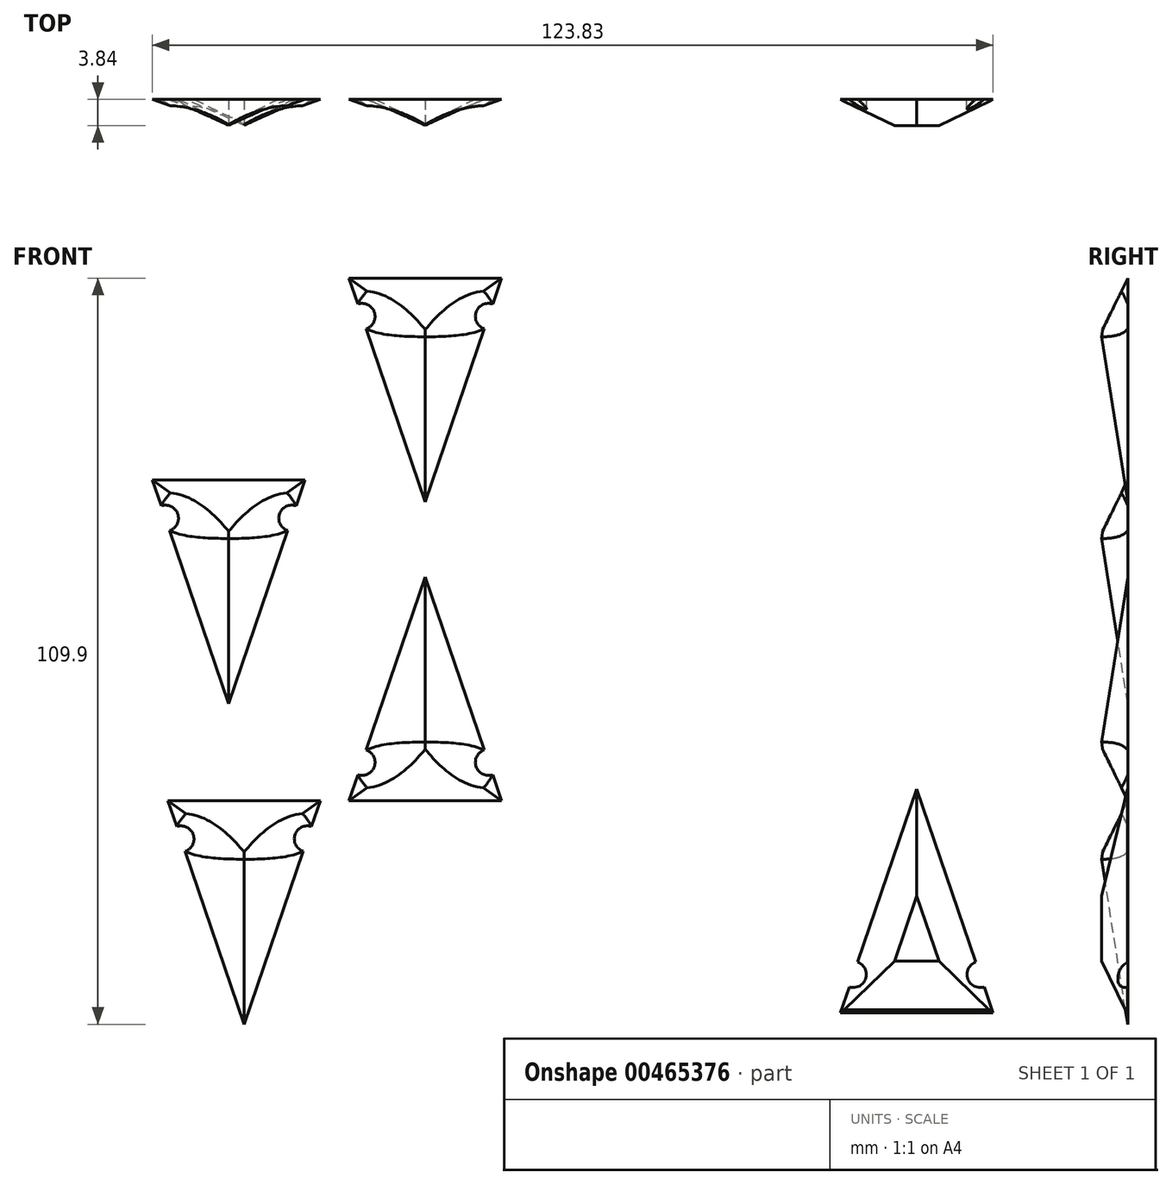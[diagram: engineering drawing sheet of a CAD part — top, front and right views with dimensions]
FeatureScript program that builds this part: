
annotation { "Feature Type Name" : "Feature", "Feature Type Description" : "" }
export const myFeature = defineFeature(function(context is Context, id is Id, definition is map)
    precondition{}
    {
        {
            var Q0;
            Q0=qCreatedBy(makeId("Front.planeOp"),FACE);
            var sketch = newSketch(context, id + "F0", { "sketchPlane" : qUnion([Q0])});
            skLineSegment(sketch, "E0.0", {"start": v(51.45, -35.1) * mm, "end": v(28.97, -35.1) * mm});
            skPoint(sketch, "E0.0.midPoint", {"position": v(40.22, -35.1) * mm});
            skPoint(sketch, "E0.cCircle.center.orphan", {"position": v(40.22, -24.11) * mm});
            skLineSegment(sketch, "E1", {"start": v(40.22, -2.16) * mm, "end": v(31.52, -27.63) * mm});
            skLineSegment(sketch, "E2", {"start": v(40.22, -2.16) * mm, "end": v(48.9, -27.63) * mm});
            skPoint(sketch, "E3.orphan", {"position": v(59.23, -35.1) * mm});
            skPoint(sketch, "E4.orphan", {"position": v(21.2, -35.1) * mm});
            skArc(sketch, "E5", {"start": v(30.27, -31.27) * mm, "mid": v(32.72, -30.07) * mm, "end": v(31.52, -27.63) * mm});
            skArc(sketch, "E6", {"start": v(48.9, -27.63) * mm, "mid": v(47.7, -30.07) * mm, "end": v(50.15, -31.27) * mm});
            skLineSegment(sketch, "E7.trimOffspring", {"start": v(50.15, -31.27) * mm, "end": v(51.45, -35.1) * mm});
            skLineSegment(sketch, "E8.trimOffspring", {"start": v(30.27, -31.27) * mm, "end": v(28.97, -35.1) * mm});
            skSolve(sketch);
        }
        {
            var Q0;
            Q0=makeQuery(id+"F0.imprint","IMPRINT",FACE,{"disambiguationData":[TD([[makeQuery(id+"F0.imprint","IMPRINT",EDGE,{"derivedFrom":sQuery(id+"F0.wireOp",EDGE,"E0.0")}),-1.0]])]});
            extrude(context, id + "F1", {"entities" : qUnion([Q0]), "depth" : 3.84 * mm, "offsetDistance" : 25.4 * mm, "hasDraft" : true, "draftAngle" : 64 * degree, "draftPullDirection" : true});
        }
        {
            var Q0;
            Q0=makeQuery(id+"F1.opExtrude","CAP_FACE",FACE,{"disambiguationData":[OSD([sQuery(id+"F0.wireOp",EDGE,"E0.0"),sQuery(id+"F0.wireOp",EDGE,"E1"),sQuery(id+"F0.wireOp",EDGE,"E2"),sQuery(id+"F0.wireOp",EDGE,"E5"),sQuery(id+"F0.wireOp",EDGE,"E6"),sQuery(id+"F0.wireOp",EDGE,"E7.trimOffspring"),sQuery(id+"F0.wireOp",EDGE,"E8.trimOffspring")])],"isStart":true});
            extrude(context, id + "F2", {"entities" : qUnion([Q0]), "depth" : 3.84 * mm, "offsetDistance" : 25.4 * mm, "hasDraft" : true, "draftAngle" : 64 * degree, "draftPullDirection" : true});
        }
        {
            var Q0;
            Q0=makeQuery(id+"F2.opExtrude","SWEPT_BODY",BODY,{"disambiguationData":[OSD([sQuery(id+"F0.wireOp",EDGE,"E0.0"),sQuery(id+"F0.wireOp",EDGE,"E1"),sQuery(id+"F0.wireOp",EDGE,"E2"),sQuery(id+"F0.wireOp",EDGE,"E5"),sQuery(id+"F0.wireOp",EDGE,"E6"),sQuery(id+"F0.wireOp",EDGE,"E7.trimOffspring"),sQuery(id+"F0.wireOp",EDGE,"E8.trimOffspring")])]});
            transform(context, id + "F3", {"entities" : qUnion([Q0]), "transformType" : TransformType.TRANSLATION_3D, "dx" : -26.67 * mm, "dy" : 0 * mm, "dz" : 0 * mm, "makeCopy" : false});
        }
        {
            var Q0;
            Q0=makeQuery(id+"F2.opExtrude","SWEPT_BODY",BODY,{"disambiguationData":[OSD([sQuery(id+"F0.wireOp",EDGE,"E0.0"),sQuery(id+"F0.wireOp",EDGE,"E1"),sQuery(id+"F0.wireOp",EDGE,"E2"),sQuery(id+"F0.wireOp",EDGE,"E5"),sQuery(id+"F0.wireOp",EDGE,"E6"),sQuery(id+"F0.wireOp",EDGE,"E7.trimOffspring"),sQuery(id+"F0.wireOp",EDGE,"E8.trimOffspring")])]});
            var Q1;
            Q1=makeQuery(id+"F2.opExtrude","CAP_EDGE",EDGE,{"disambiguationData":[OSD([sQuery(id+"F0.wireOp",EDGE,"E0.0")])],"isStart":true});
            transform(context, id + "F4", {"entities" : qUnion([Q0]), "transformType" : TransformType.ROTATION, "transformAxis" : qUnion([Q1]), "angle" : 180 * degree, "makeCopy" : false});
        }
        {
            var Q0;
            Q0=makeQuery(id+"F1.opExtrude","CAP_FACE",FACE,{"disambiguationData":[OSD([sQuery(id+"F0.wireOp",EDGE,"E0.0"),sQuery(id+"F0.wireOp",EDGE,"E1"),sQuery(id+"F0.wireOp",EDGE,"E2"),sQuery(id+"F0.wireOp",EDGE,"E5"),sQuery(id+"F0.wireOp",EDGE,"E6"),sQuery(id+"F0.wireOp",EDGE,"E7.trimOffspring"),sQuery(id+"F0.wireOp",EDGE,"E8.trimOffspring")])],"isStart":true});
            extrude(context, id + "F5", {"entities" : qUnion([Q0]), "depth" : 3.84 * mm, "offsetDistance" : 25.4 * mm, "hasDraft" : true, "draftAngle" : 64 * degree, "draftPullDirection" : true});
        }
        {
            var Q0;
            Q0=makeQuery(id+"F5.opExtrude","SWEPT_BODY",BODY,{"disambiguationData":[OSD([sQuery(id+"F0.wireOp",EDGE,"E0.0"),sQuery(id+"F0.wireOp",EDGE,"E1"),sQuery(id+"F0.wireOp",EDGE,"E2"),sQuery(id+"F0.wireOp",EDGE,"E5"),sQuery(id+"F0.wireOp",EDGE,"E6"),sQuery(id+"F0.wireOp",EDGE,"E7.trimOffspring"),sQuery(id+"F0.wireOp",EDGE,"E8.trimOffspring")])]});
            transform(context, id + "F6", {"entities" : qUnion([Q0]), "transformType" : TransformType.TRANSLATION_3D, "dx" : -28.96 * mm, "dy" : 0 * mm, "dz" : 47.24 * mm, "makeCopy" : false});
        }
        {
            var Q0;
            Q0=makeQuery(id+"F5.opExtrude","SWEPT_BODY",BODY,{"disambiguationData":[OSD([sQuery(id+"F0.wireOp",EDGE,"E0.0"),sQuery(id+"F0.wireOp",EDGE,"E1"),sQuery(id+"F0.wireOp",EDGE,"E2"),sQuery(id+"F0.wireOp",EDGE,"E5"),sQuery(id+"F0.wireOp",EDGE,"E6"),sQuery(id+"F0.wireOp",EDGE,"E7.trimOffspring"),sQuery(id+"F0.wireOp",EDGE,"E8.trimOffspring")])]});
            var Q1;
            Q1=makeQuery(id+"F5.opExtrude","CAP_EDGE",EDGE,{"disambiguationData":[OSD([sQuery(id+"F0.wireOp",EDGE,"E0.0")])],"isStart":true});
            transform(context, id + "F7", {"entities" : qUnion([Q0]), "transformType" : TransformType.ROTATION, "transformAxis" : qUnion([Q1]), "angle" : 180 * degree, "makeCopy" : false});
        }
        {
            var Q0;
            Q0=makeQuery(id+"F1.opExtrude","CAP_FACE",FACE,{"disambiguationData":[OSD([sQuery(id+"F0.wireOp",EDGE,"E0.0"),sQuery(id+"F0.wireOp",EDGE,"E1"),sQuery(id+"F0.wireOp",EDGE,"E2"),sQuery(id+"F0.wireOp",EDGE,"E5"),sQuery(id+"F0.wireOp",EDGE,"E6"),sQuery(id+"F0.wireOp",EDGE,"E7.trimOffspring"),sQuery(id+"F0.wireOp",EDGE,"E8.trimOffspring")])],"isStart":true});
            extrude(context, id + "F8", {"entities" : qUnion([Q0]), "depth" : 3.84 * mm, "offsetDistance" : 25.4 * mm, "hasDraft" : true, "draftAngle" : 64 * degree, "draftPullDirection" : true});
        }
        {
            var Q0;
            Q0=makeQuery(id+"F8.opExtrude","SWEPT_BODY",BODY,{"disambiguationData":[OSD([sQuery(id+"F0.wireOp",EDGE,"E0.0"),sQuery(id+"F0.wireOp",EDGE,"E1"),sQuery(id+"F0.wireOp",EDGE,"E2"),sQuery(id+"F0.wireOp",EDGE,"E5"),sQuery(id+"F0.wireOp",EDGE,"E6"),sQuery(id+"F0.wireOp",EDGE,"E7.trimOffspring"),sQuery(id+"F0.wireOp",EDGE,"E8.trimOffspring")])]});
            transform(context, id + "F9", {"entities" : qUnion([Q0]), "transformType" : TransformType.TRANSLATION_3D, "dx" : 0 * mm, "dy" : 0 * mm, "dz" : 76.96 * mm, "makeCopy" : false});
        }
        {
            var Q0;
            Q0=makeQuery(id+"F8.opExtrude","SWEPT_BODY",BODY,{"disambiguationData":[OSD([sQuery(id+"F0.wireOp",EDGE,"E0.0"),sQuery(id+"F0.wireOp",EDGE,"E1"),sQuery(id+"F0.wireOp",EDGE,"E2"),sQuery(id+"F0.wireOp",EDGE,"E5"),sQuery(id+"F0.wireOp",EDGE,"E6"),sQuery(id+"F0.wireOp",EDGE,"E7.trimOffspring"),sQuery(id+"F0.wireOp",EDGE,"E8.trimOffspring")])]});
            var Q1;
            Q1=makeQuery(id+"F8.opExtrude","CAP_EDGE",EDGE,{"disambiguationData":[OSD([sQuery(id+"F0.wireOp",EDGE,"E0.0")])],"isStart":true});
            transform(context, id + "F10", {"entities" : qUnion([Q0]), "transformType" : TransformType.ROTATION, "transformAxis" : qUnion([Q1]), "angle" : 180 * degree, "makeCopy" : false});
        }
        {
            var Q0;
            Q0=makeQuery(id+"F1.opExtrude","SWEPT_BODY",BODY,{"disambiguationData":[OSD([sQuery(id+"F0.wireOp",EDGE,"E0.0"),sQuery(id+"F0.wireOp",EDGE,"E1"),sQuery(id+"F0.wireOp",EDGE,"E2"),sQuery(id+"F0.wireOp",EDGE,"E5"),sQuery(id+"F0.wireOp",EDGE,"E6"),sQuery(id+"F0.wireOp",EDGE,"E7.trimOffspring"),sQuery(id+"F0.wireOp",EDGE,"E8.trimOffspring")])]});
            var Q1;
            Q1=makeQuery(id+"F2.opExtrude","SWEPT_BODY",BODY,{"disambiguationData":[OSD([sQuery(id+"F0.wireOp",EDGE,"E0.0"),sQuery(id+"F0.wireOp",EDGE,"E1"),sQuery(id+"F0.wireOp",EDGE,"E2"),sQuery(id+"F0.wireOp",EDGE,"E5"),sQuery(id+"F0.wireOp",EDGE,"E6"),sQuery(id+"F0.wireOp",EDGE,"E7.trimOffspring"),sQuery(id+"F0.wireOp",EDGE,"E8.trimOffspring")])]});
            var Q2;
            Q2=makeQuery(id+"F5.opExtrude","SWEPT_BODY",BODY,{"disambiguationData":[OSD([sQuery(id+"F0.wireOp",EDGE,"E0.0"),sQuery(id+"F0.wireOp",EDGE,"E1"),sQuery(id+"F0.wireOp",EDGE,"E2"),sQuery(id+"F0.wireOp",EDGE,"E5"),sQuery(id+"F0.wireOp",EDGE,"E6"),sQuery(id+"F0.wireOp",EDGE,"E7.trimOffspring"),sQuery(id+"F0.wireOp",EDGE,"E8.trimOffspring")])]});
            var Q3;
            Q3=makeQuery(id+"F8.opExtrude","SWEPT_BODY",BODY,{"disambiguationData":[OSD([sQuery(id+"F0.wireOp",EDGE,"E0.0"),sQuery(id+"F0.wireOp",EDGE,"E1"),sQuery(id+"F0.wireOp",EDGE,"E2"),sQuery(id+"F0.wireOp",EDGE,"E5"),sQuery(id+"F0.wireOp",EDGE,"E6"),sQuery(id+"F0.wireOp",EDGE,"E7.trimOffspring"),sQuery(id+"F0.wireOp",EDGE,"E8.trimOffspring")])]});
            transform(context, id + "F11", {"entities" : qUnion([Q0, Q1, Q2, Q3]), "transformType" : TransformType.TRANSLATION_3D, "dx" : -72.39 * mm, "dy" : 0 * mm, "dz" : 31.24 * mm, "makeCopy" : false});
        }
        {
            var Q0;
            Q0=makeQuery(id+"F0.imprint","IMPRINT",FACE,{"disambiguationData":[TD([[makeQuery(id+"F0.imprint","IMPRINT",EDGE,{"derivedFrom":sQuery(id+"F0.wireOp",EDGE,"E0.0")}),-1.0]])]});
            extrude(context, id + "F12", {"entities" : qUnion([Q0]), "depth" : 3.84 * mm, "offsetDistance" : 25.4 * mm});
        }
        {
            var Q0;
            Q0=makeQuery(id+"F12.opExtrude","CAP_EDGE",EDGE,{"disambiguationData":[OSD([sQuery(id+"F0.wireOp",EDGE,"E1")])],"isStart":false});
            var Q1;
            Q1=makeQuery(id+"F12.opExtrude","CAP_EDGE",EDGE,{"disambiguationData":[OSD([sQuery(id+"F0.wireOp",EDGE,"E2")])],"isStart":false});
            var Q2;
            Q2=makeQuery(id+"F12.opExtrude","CAP_EDGE",EDGE,{"disambiguationData":[OSD([sQuery(id+"F0.wireOp",EDGE,"E0.0")])],"isStart":false});
            chamfer(context, id + "F13", {"entities" : qUnion([Q0, Q1, Q2]), "chamferType" : ChamferType.OFFSET_ANGLE, "width" : 5.08 * mm, "oppositeDirection" : false, "angle" : 37 * degree, "tangentPropagation" : true});
        }
        {
            var Q0;
            {var subQ0=sQuery(id+"F0.wireOp",EDGE,"E0.0");Q0=makeQuery(id+"F13.opChamfer","BLEND_EDGE",EDGE,{"blendedFrom":[makeQuery(id+"F12.opExtrude","CAP_EDGE",EDGE,{"disambiguationData":[OSD([subQ0])],"isStart":false}),makeQuery(id+"F12.opExtrude","CAP_FACE",FACE,{"disambiguationData":[OSD([subQ0,sQuery(id+"F0.wireOp",EDGE,"E1"),sQuery(id+"F0.wireOp",EDGE,"E2"),sQuery(id+"F0.wireOp",EDGE,"E5"),sQuery(id+"F0.wireOp",EDGE,"E6"),sQuery(id+"F0.wireOp",EDGE,"E7.trimOffspring"),sQuery(id+"F0.wireOp",EDGE,"E8.trimOffspring")])],"isStart":false})],"blendedInto":[makeQuery(id+"F12.opExtrude","CAP_FACE",FACE,{"disambiguationData":[OSD([subQ0,sQuery(id+"F0.wireOp",EDGE,"E1"),sQuery(id+"F0.wireOp",EDGE,"E2"),sQuery(id+"F0.wireOp",EDGE,"E5"),sQuery(id+"F0.wireOp",EDGE,"E6"),sQuery(id+"F0.wireOp",EDGE,"E7.trimOffspring"),sQuery(id+"F0.wireOp",EDGE,"E8.trimOffspring")])],"isStart":false})]});}
            chamfer(context, id + "F14", {"entities" : qUnion([Q0]), "chamferType" : ChamferType.OFFSET_ANGLE, "width" : 2.54 * mm, "oppositeDirection" : false, "angle" : 26 * degree, "tangentPropagation" : true});
        }
    });
